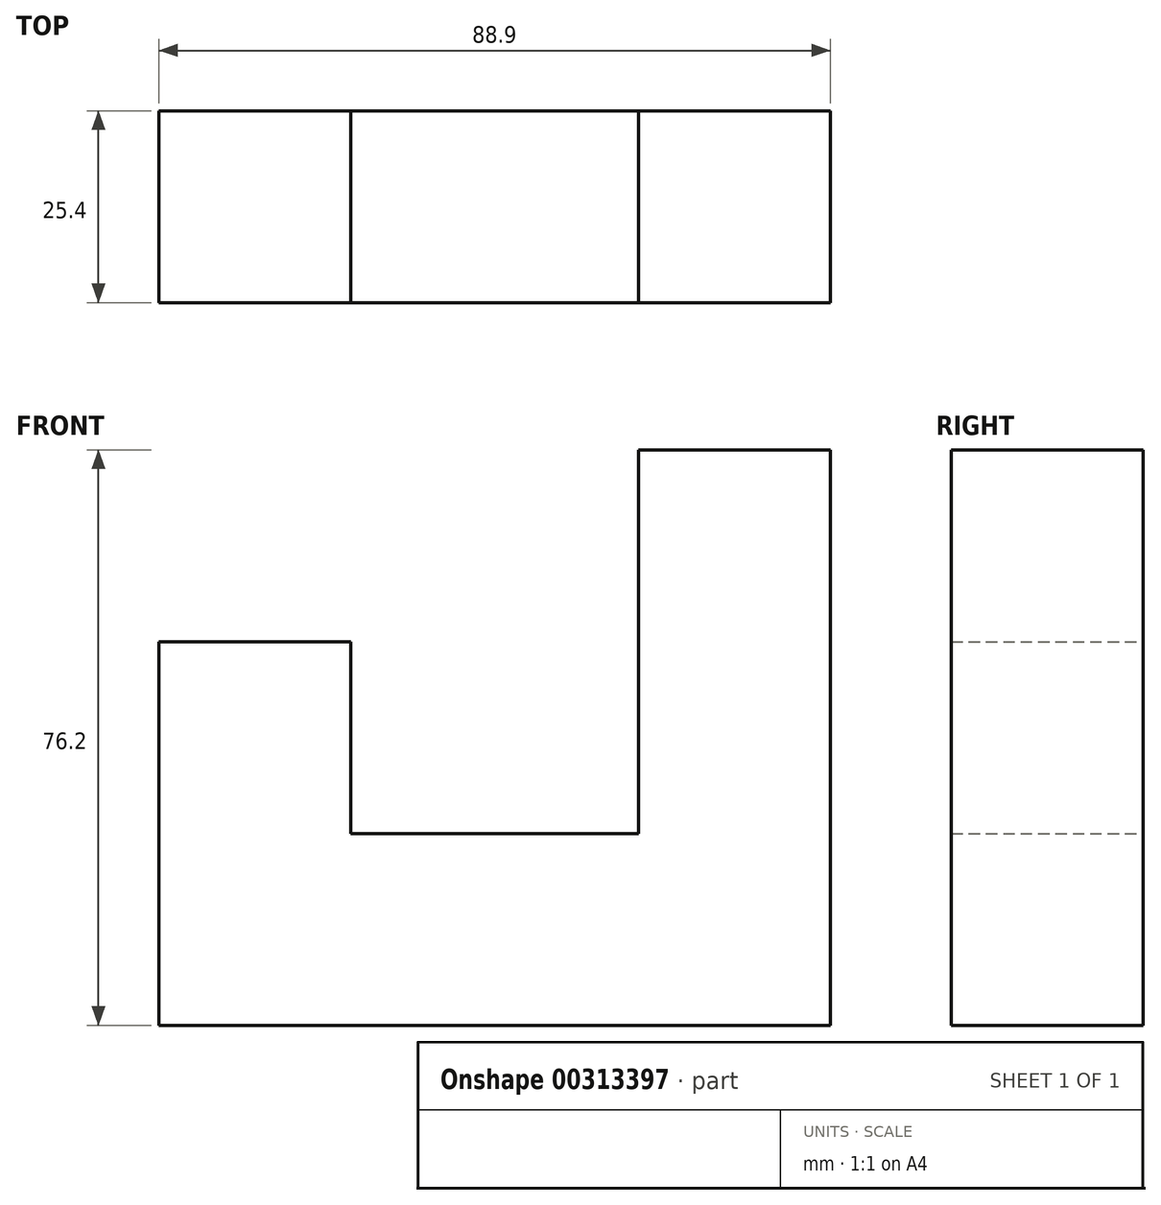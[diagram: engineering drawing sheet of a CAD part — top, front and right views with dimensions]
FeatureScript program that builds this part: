
annotation { "Feature Type Name" : "Feature", "Feature Type Description" : "" }
export const myFeature = defineFeature(function(context is Context, id is Id, definition is map)
    precondition{}
    {
        {
            var Q0;
            Q0=qCreatedBy(makeId("Front.planeOp"),FACE);
            var sketch = newSketch(context, id + "F0", { "sketchPlane" : qUnion([Q0])});
            skLineSegment(sketch, "E0", {"start": v(-37.16, -43.3) * mm, "end": v(51.74, -43.3) * mm});
            skLineSegment(sketch, "E1", {"start": v(51.74, -43.3) * mm, "end": v(51.74, 32.9) * mm});
            skLineSegment(sketch, "E2", {"start": v(51.74, 32.9) * mm, "end": v(26.34, 32.9) * mm});
            skLineSegment(sketch, "E3", {"start": v(26.34, 32.9) * mm, "end": v(26.34, -17.9) * mm});
            skLineSegment(sketch, "E4", {"start": v(26.34, -17.9) * mm, "end": v(-11.76, -17.9) * mm});
            skLineSegment(sketch, "E5", {"start": v(-11.76, -17.9) * mm, "end": v(-11.76, 7.5) * mm});
            skLineSegment(sketch, "E6", {"start": v(-11.76, 7.5) * mm, "end": v(-37.16, 7.5) * mm});
            skLineSegment(sketch, "E7", {"start": v(-37.16, 7.5) * mm, "end": v(-37.16, -43.3) * mm});
            skSolve(sketch);
        }
        {
            var Q0;
            Q0=makeQuery(id+"F0.imprint","IMPRINT",FACE,{"disambiguationData":[TD([[makeQuery(id+"F0.imprint","IMPRINT",EDGE,{"derivedFrom":sQuery(id+"F0.wireOp",EDGE,"E0")}),1.0]])]});
            extrude(context, id + "F1", {"entities" : qUnion([Q0]), "depth" : 25.4 * mm});
        }
    });
